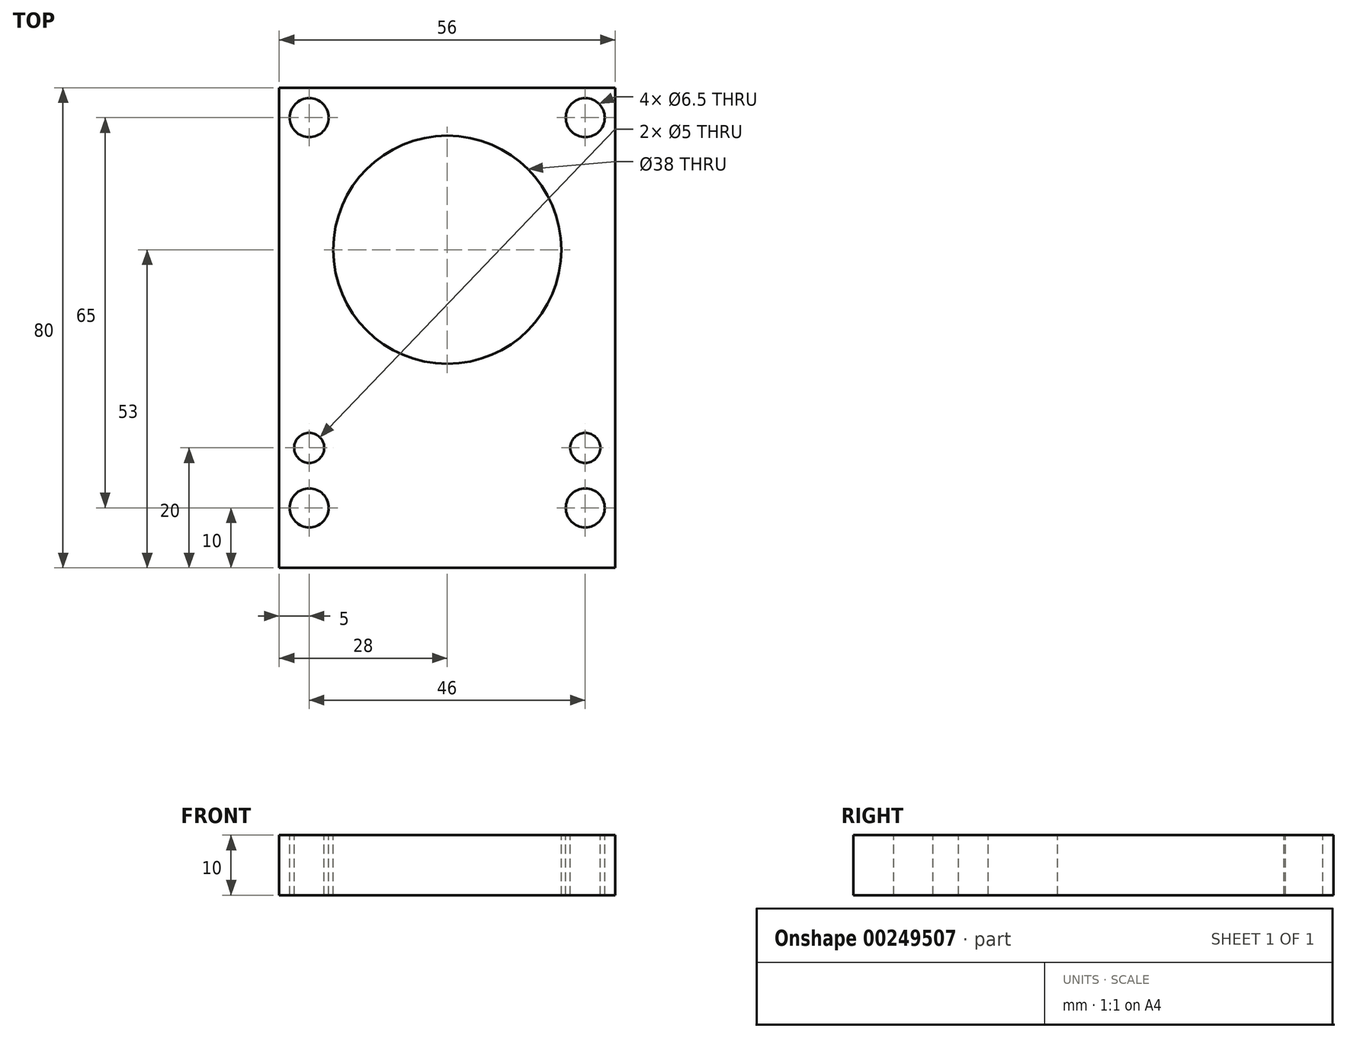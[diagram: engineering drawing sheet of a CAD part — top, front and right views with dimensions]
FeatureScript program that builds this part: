
annotation { "Feature Type Name" : "Feature", "Feature Type Description" : "" }
export const myFeature = defineFeature(function(context is Context, id is Id, definition is map)
    precondition{}
    {
        {
            var Q0;
            Q0=qCreatedBy(makeId("Top.planeOp"),FACE);
            var sketch = newSketch(context, id + "F0", { "sketchPlane" : qUnion([Q0])});
            skLineSegment(sketch, "E0.bottom", {"start": v(-28, 27) * mm, "end": v(28, 27) * mm});
            skLineSegment(sketch, "E0.top", {"start": v(-28, -53) * mm, "end": v(28, -53) * mm});
            skLineSegment(sketch, "E0.left", {"start": v(-28, 27) * mm, "end": v(-28, -53) * mm});
            skLineSegment(sketch, "E0.right", {"start": v(28, 27) * mm, "end": v(28, -53) * mm});
            skSolve(sketch);
        }
        {
            var Q0;
            Q0 = qSketchRegion(id + "F0", true);
            extrude(context, id + "F1", {"entities" : qUnion([Q0]), "depth" : 10 * mm});
        }
        {
            var Q0;
            Q0=makeQuery(id+"F1.opExtrude","CAP_FACE",FACE,{"disambiguationData":[OSD([sQuery(id+"F0.wireOp",EDGE,"E0.bottom"),sQuery(id+"F0.wireOp",EDGE,"E0.top"),sQuery(id+"F0.wireOp",EDGE,"E0.left"),sQuery(id+"F0.wireOp",EDGE,"E0.right")])],"isStart":false});
            var sketch = newSketch(context, id + "F2", { "sketchPlane" : qUnion([Q0])});
            skCircle(sketch, "E1", {"center": v(0, 0) * mm, "radius": 19 * mm});
            skSolve(sketch);
        }
        {
            var Q0;
            Q0 = qSketchRegion(id + "F2", true);
            extrude(context, id + "F3", {"entities" : qUnion([Q0]), "operationType" : NewBodyOperationType.REMOVE, "endBound" : BoundingType.THROUGH_ALL, "oppositeDirection" : true, "depth" : 25 * mm});
        }
        {
            var Q0;
            Q0=makeQuery(id+"F1.opExtrude","CAP_FACE",FACE,{"disambiguationData":[OSD([sQuery(id+"F0.wireOp",EDGE,"E0.bottom"),sQuery(id+"F0.wireOp",EDGE,"E0.top"),sQuery(id+"F0.wireOp",EDGE,"E0.left"),sQuery(id+"F0.wireOp",EDGE,"E0.right")])],"isStart":false});
            var sketch = newSketch(context, id + "F4", { "sketchPlane" : qUnion([Q0])});
            skCircle(sketch, "E2", {"center": v(-23, 22) * mm, "radius": 3.25 * mm});
            skCircle(sketch, "E3.0.1.0", {"center": v(-23, -43) * mm, "radius": 3.25 * mm});
            skCircle(sketch, "E3.1.0.0", {"center": v(23, 22) * mm, "radius": 3.25 * mm});
            skCircle(sketch, "E3.1.1.0", {"center": v(23, -43) * mm, "radius": 3.25 * mm});
            skLineSegment(sketch, "E3.direction1", {"start": v(-23, 22) * mm, "end": v(23, 22) * mm, "construction": true});
            skLineSegment(sketch, "E3.direction2", {"start": v(-23, 22) * mm, "end": v(-23, -43) * mm, "construction": true});
            skSolve(sketch);
        }
        {
            var Q0;
            Q0 = qSketchRegion(id + "F4", true);
            extrude(context, id + "F5", {"entities" : qUnion([Q0]), "operationType" : NewBodyOperationType.REMOVE, "endBound" : BoundingType.THROUGH_ALL, "oppositeDirection" : true, "depth" : 25 * mm});
        }
        {
            var Q0;
            Q0=makeQuery(id+"F1.opExtrude","CAP_FACE",FACE,{"disambiguationData":[OSD([sQuery(id+"F0.wireOp",EDGE,"E0.bottom"),sQuery(id+"F0.wireOp",EDGE,"E0.top"),sQuery(id+"F0.wireOp",EDGE,"E0.left"),sQuery(id+"F0.wireOp",EDGE,"E0.right")])],"isStart":false});
            var sketch = newSketch(context, id + "F6", { "sketchPlane" : qUnion([Q0])});
            skCircle(sketch, "E4", {"center": v(-23, -33) * mm, "radius": 2.5 * mm});
            skCircle(sketch, "E5", {"center": v(23, -33) * mm, "radius": 2.5 * mm});
            skSolve(sketch);
        }
        {
            var Q0;
            Q0 = qSketchRegion(id + "F6", true);
            extrude(context, id + "F7", {"entities" : qUnion([Q0]), "operationType" : NewBodyOperationType.REMOVE, "endBound" : BoundingType.THROUGH_ALL, "oppositeDirection" : true, "depth" : 25 * mm});
        }
    });
